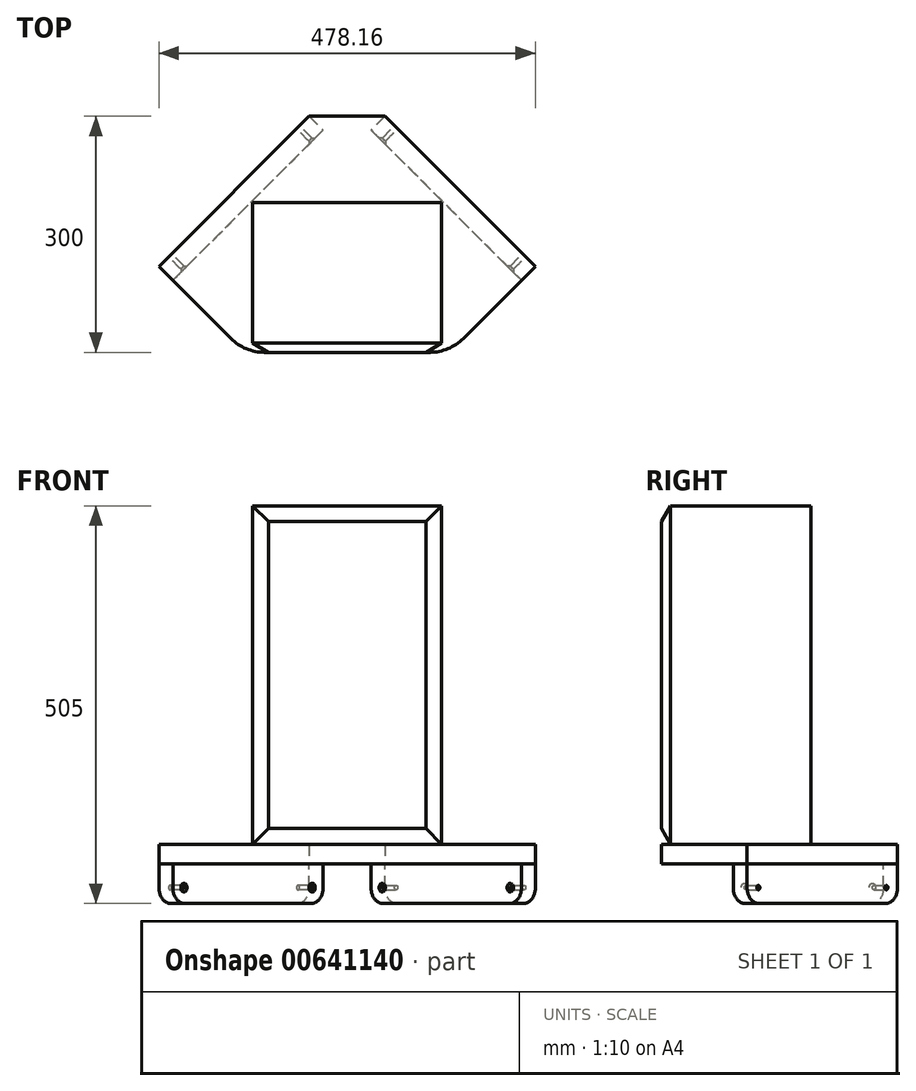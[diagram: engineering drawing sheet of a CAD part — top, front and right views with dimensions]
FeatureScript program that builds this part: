
annotation { "Feature Type Name" : "Feature", "Feature Type Description" : "" }
export const myFeature = defineFeature(function(context is Context, id is Id, definition is map)
    precondition{}
    {
        {
            var Q0;
            Q0=qCreatedBy(makeId("Top.planeOp"),FACE);
            var sketch = newSketch(context, id + "F0", { "sketchPlane" : qUnion([Q0])});
            skLineSegment(sketch, "E0", {"start": v(-48.16, 0) * mm, "end": v(48.16, 0) * mm});
            skLineSegment(sketch, "E1", {"start": v(48.16, 0) * mm, "end": v(239.08, -190.92) * mm});
            skLineSegment(sketch, "E2", {"start": v(239.08, -190.92) * mm, "end": v(130, -300) * mm});
            skLineSegment(sketch, "E3", {"start": v(130, -300) * mm, "end": v(-130, -300) * mm});
            skLineSegment(sketch, "E4", {"start": v(-130, -300) * mm, "end": v(-239.08, -190.92) * mm});
            skLineSegment(sketch, "E5", {"start": v(-239.08, -190.92) * mm, "end": v(-48.16, 0) * mm});
            skLineSegment(sketch, "E6", {"start": v(0, 0) * mm, "end": v(0, -600) * mm, "construction": true});
            skPoint(sketch, "E7", {"position": v(0, -300) * mm});
            skLineSegment(sketch, "E8", {"start": v(120, -300) * mm, "end": v(120, -110) * mm, "construction": true});
            skLineSegment(sketch, "E9", {"start": v(120, -110) * mm, "end": v(-120, -110) * mm, "construction": true});
            skLineSegment(sketch, "E10", {"start": v(-120, -110) * mm, "end": v(-120, -300) * mm, "construction": true});
            skPoint(sketch, "E11", {"position": v(0, -110) * mm});
            skSolve(sketch);
        }
        {
            var Q0;
            Q0 = qSketchRegion(id + "F0", true);
            extrude(context, id + "F1", {"entities" : qUnion([Q0]), "depth" : 25 * mm, "offsetDistance" : 25 * mm});
        }
        {
            var Q0;
            Q0=makeQuery(id+"F1.opExtrude","CAP_FACE",FACE,{"disambiguationData":[OSD([sQuery(id+"F0.wireOp",EDGE,"E0"),sQuery(id+"F0.wireOp",EDGE,"E1"),sQuery(id+"F0.wireOp",EDGE,"E2"),sQuery(id+"F0.wireOp",EDGE,"E3"),sQuery(id+"F0.wireOp",EDGE,"E4"),sQuery(id+"F0.wireOp",EDGE,"E5")])],"isStart":true});
            var sketch = newSketch(context, id + "F2", { "sketchPlane" : qUnion([Q0])});
            skLineSegment(sketch, "E12", {"start": v(-239.08, 190.92) * mm, "end": v(-48.16, 0) * mm});
            skLineSegment(sketch, "E13", {"start": v(-48.16, 0) * mm, "end": v(-30.48, 17.68) * mm});
            skLineSegment(sketch, "E14", {"start": v(-30.48, 17.68) * mm, "end": v(-221.4, 208.6) * mm});
            skLineSegment(sketch, "E15", {"start": v(-221.4, 208.6) * mm, "end": v(-239.08, 190.92) * mm});
            skSolve(sketch);
        }
        {
            var Q0;
            Q0 = qSketchRegion(id + "F2", true);
            extrude(context, id + "F3", {"entities" : qUnion([Q0]), "depth" : 50 * mm, "offsetDistance" : 25 * mm});
        }
        {
            var Q0;
            Q0=makeQuery(id+"F3.opExtrude","SWEPT_FACE",FACE,{"disambiguationData":[OSD([sQuery(id+"F2.wireOp",EDGE,"E14")])]});
            var sketch = newSketch(context, id + "F4", { "sketchPlane" : qUnion([Q0])});
            skPoint(sketch, "E16", {"position": v(-284.06, -30) * mm});
            skPoint(sketch, "E17", {"position": v(-54.06, -30) * mm});
            skSolve(sketch);
        }
        {
            var Q0;
            Q0=sQuery(id+"F4.wireOp",VERTEX,"E16");
            var Q1;
            Q1=sQuery(id+"F4.wireOp",VERTEX,"E17");
            var Q2;
            Q2=makeQuery(id+"F3.opExtrude","SWEPT_BODY",BODY,{"disambiguationData":[OSD([sQuery(id+"F2.wireOp",EDGE,"E12"),sQuery(id+"F2.wireOp",EDGE,"E13"),sQuery(id+"F2.wireOp",EDGE,"E14"),sQuery(id+"F2.wireOp",EDGE,"E15")])]});
            hole(context, id + "F5", {"style" : HoleStyle.C_SINK, "endStyle" : HoleEndStyle.THROUGH, "standardTappedOrClearance" : lookupTablePath({ "standard" : "ISO", "size" : "5.5", "type" : "Drilled" }), "standardBlindInLast" : lookupTablePath({ "standard" : "ISO", "size" : "5.5", "type" : "Drilled" }), "holeDiameter" : 5.5 * mm, "cSinkDiameter" : 11.2 * mm, "cSinkAngle" : 90 * degree, "majorDiameter" : 5 * mm, "isTappedThrough" : true, "tappedDepth" : 12 * mm, "tapClearance" : 3, "startFromSketch" : true, "locations" : qUnion([Q0, Q1]), "scope" : qUnion([Q2])});
        }
        {
            var Q0;
            Q0=makeQuery(id+"F3.opExtrude","CAP_EDGE",EDGE,{"disambiguationData":[OSD([sQuery(id+"F2.wireOp",EDGE,"E15")])],"isStart":false});
            var Q1;
            Q1=makeQuery(id+"F3.opExtrude","CAP_EDGE",EDGE,{"disambiguationData":[OSD([sQuery(id+"F2.wireOp",EDGE,"E13")])],"isStart":false});
            fillet(context, id + "F6", {"entities" : qUnion([Q0, Q1]), "radius" : 20 * mm, "tangentPropagation" : true, "allowEdgeOverflow" : false});
        }
        {
            var Q0;
            Q0=makeQuery(id+"F3.opExtrude","SWEPT_BODY",BODY,{"disambiguationData":[OSD([sQuery(id+"F2.wireOp",EDGE,"E12"),sQuery(id+"F2.wireOp",EDGE,"E13"),sQuery(id+"F2.wireOp",EDGE,"E14"),sQuery(id+"F2.wireOp",EDGE,"E15")])]});
            var Q1;
            Q1=qCreatedBy(makeId("Right.planeOp"),FACE);
            mirror(context, id + "F7", {"entities" : qUnion([Q0]), "mirrorPlane" : qUnion([Q1])});
        }
        {
            var Q0;
            Q0=makeQuery(id+"F1.opExtrude","CAP_FACE",FACE,{"disambiguationData":[OSD([sQuery(id+"F0.wireOp",EDGE,"E0"),sQuery(id+"F0.wireOp",EDGE,"E1"),sQuery(id+"F0.wireOp",EDGE,"E2"),sQuery(id+"F0.wireOp",EDGE,"E3"),sQuery(id+"F0.wireOp",EDGE,"E4"),sQuery(id+"F0.wireOp",EDGE,"E5")])],"isStart":false});
            var sketch = newSketch(context, id + "F8", { "sketchPlane" : qUnion([Q0])});
            skLineSegment(sketch, "E18.0", {"start": v(-120, -110) * mm, "end": v(-120, -300) * mm});
            skLineSegment(sketch, "E18.1", {"start": v(120, -300) * mm, "end": v(120, -110) * mm});
            skLineSegment(sketch, "E18.2", {"start": v(120, -110) * mm, "end": v(-120, -110) * mm});
            skLineSegment(sketch, "E18.3", {"start": v(120, -300) * mm, "end": v(-120, -300) * mm});
            skPoint(sketch, "E19.orphan", {"position": v(-130, -300) * mm});
            skPoint(sketch, "E20.orphan", {"position": v(130, -300) * mm});
            skSolve(sketch);
        }
        {
            var Q0;
            Q0=makeQuery(id+"F8.imprint","IMPRINT",FACE,{"disambiguationData":[TD([[makeQuery(id+"F8.imprint","IMPRINT",EDGE,{"derivedFrom":sQuery(id+"F8.wireOp",EDGE,"E18.0")}),1.0]])]});
            extrude(context, id + "F9", {"entities" : qUnion([Q0]), "depth" : 430 * mm, "offsetDistance" : 25 * mm});
        }
        {
            var Q0;
            Q0=makeQuery(id+"F9.opExtrude","SWEPT_FACE",FACE,{"disambiguationData":[OSD([sQuery(id+"F8.wireOp",EDGE,"E18.3")])]});
            chamfer(context, id + "F10", {"entities" : qUnion([Q0]), "chamferType" : ChamferType.OFFSET_ANGLE, "width" : 20 * mm, "oppositeDirection" : false, "angle" : 30 * degree, "tangentPropagation" : true});
        }
        {
            var Q0;
            Q0=makeQuery(id+"F1.opExtrude","SWEPT_EDGE",EDGE,{"disambiguationData":[OSD([sQuery(id+"F0.wireOp",EDGE,"E2"),sQuery(id+"F0.wireOp",EDGE,"E3")])]});
            var Q1;
            Q1=makeQuery(id+"F1.opExtrude","SWEPT_EDGE",EDGE,{"disambiguationData":[OSD([sQuery(id+"F0.wireOp",EDGE,"E3"),sQuery(id+"F0.wireOp",EDGE,"E4")])]});
            fillet(context, id + "F11", {"entities" : qUnion([Q0, Q1]), "radius" : 60 * mm, "tangentPropagation" : true, "allowEdgeOverflow" : false});
        }
    });
